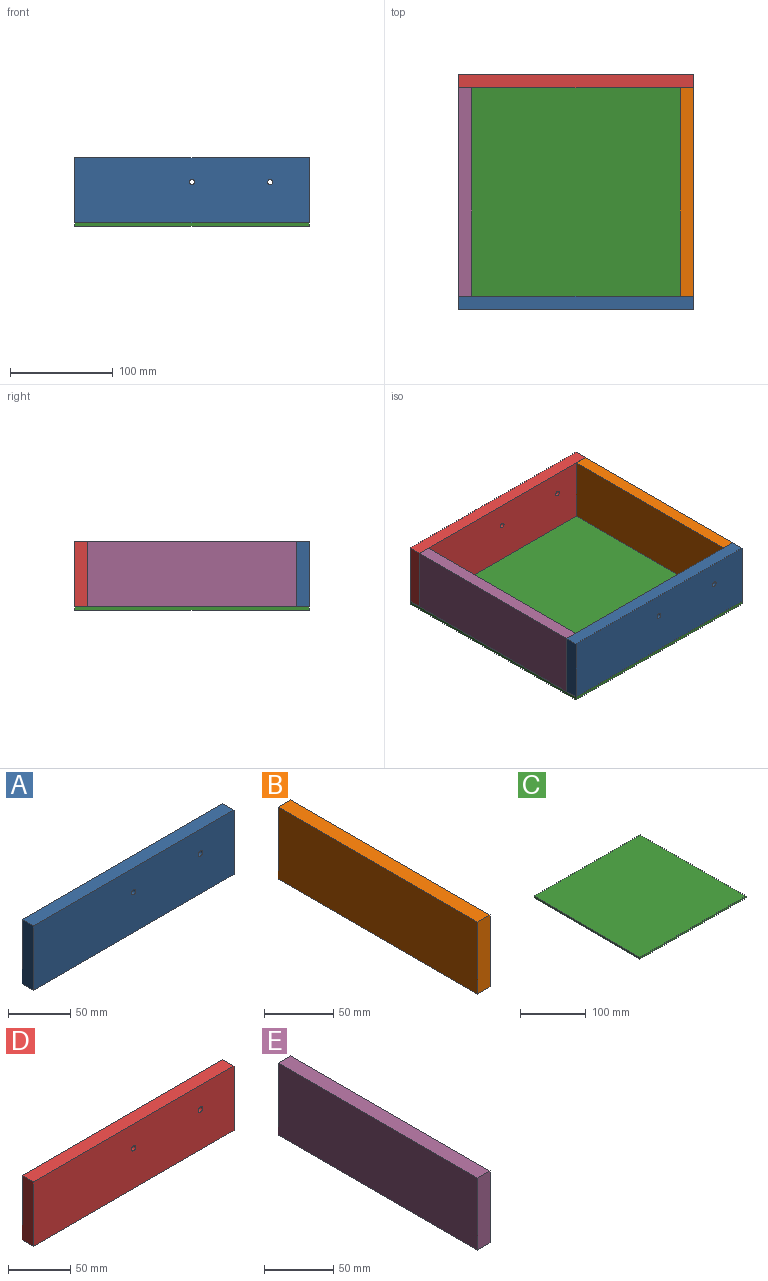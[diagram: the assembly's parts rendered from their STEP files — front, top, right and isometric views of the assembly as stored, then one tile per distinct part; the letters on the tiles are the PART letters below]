
ASSEMBLY  parts=5 mates=4
PART A: 8 faces, bbox 228.6x12.7x63.5 mm
  f0: plane 228.6x63.5mm, normal (0,1,0), area 14476.8mm2, adj f1,f3,f4,f5,f6,f7
  f1: plane 63.5x12.7mm, normal (-1,0,0), area 806.5mm2, adj f0,f2,f4,f5
  f2: plane 228.6x63.5mm, normal (0,-1,0), area 14476.8mm2, adj f1,f3,f4,f5,f6,f7
  f3: plane 63.5x12.7mm, normal (1,0,0), area 806.5mm2, adj f0,f2,f4,f5
  f4: plane 228.6x12.7mm, normal (0,0,1), area 2903.2mm2, adj f0,f1,f2,f3
  f5: plane 228.6x12.7mm, normal (0,0,-1), area 2903.2mm2, adj f0,f1,f2,f3
  f6: cylinder r=2.5mm len=12.7mm, axis (0,-1,0), area 199.5mm2, adj f0,f2
  f7: cylinder r=2.5mm len=12.7mm, axis (0,-1,0), area 199.5mm2, adj f0,f2
PART B: 6 faces, bbox 12.7x203.2x63.5 mm
  f0: plane 63.5x12.7mm, normal (0,1,0), area 806.5mm2, adj f1,f3,f4,f5
  f1: plane 203.2x63.5mm, normal (-1,0,0), area 12903.2mm2, adj f0,f2,f4,f5
  f2: plane 63.5x12.7mm, normal (0,-1,0), area 806.5mm2, adj f1,f3,f4,f5
  f3: plane 203.2x63.5mm, normal (1,0,0), area 12903.2mm2, adj f0,f2,f4,f5
  f4: plane 203.2x12.7mm, normal (0,0,1), area 2580.6mm2, adj f0,f1,f2,f3
  f5: plane 203.2x12.7mm, normal (0,0,-1), area 2580.6mm2, adj f0,f1,f2,f3
PART C: 6 faces, bbox 228.6x228.6x3.2 mm
  f0: plane 228.6x3.18mm, normal (0,-1,0), area 725.8mm2, adj f1,f3,f4,f5
  f1: plane 228.6x3.18mm, normal (1,0,0), area 725.8mm2, adj f0,f2,f4,f5
  f2: plane 228.6x3.18mm, normal (0,1,0), area 725.8mm2, adj f1,f3,f4,f5
  f3: plane 228.6x3.18mm, normal (-1,0,0), area 725.8mm2, adj f0,f2,f4,f5
  f4: plane 228.6x228.6mm, normal (0,0,1), area 52258mm2, adj f0,f1,f2,f3
  f5: plane 228.6x228.6mm, normal (0,0,-1), area 52258mm2, adj f0,f1,f2,f3
PART D: 8 faces, bbox 228.6x12.7x63.5 mm
  f0: plane 63.5x12.7mm, normal (-1,0,0), area 806.4mm2, adj f1,f3,f4,f5
  f1: plane 228.6x63.5mm, normal (0,-1,0), area 14476.8mm2, adj f0,f2,f4,f5,f6,f7
  f2: plane 63.5x12.7mm, normal (1,0,0), area 806.5mm2, adj f1,f3,f4,f5
  f3: plane 228.6x63.5mm, normal (0,1,0), area 14476.8mm2, adj f0,f2,f4,f5,f6,f7
  f4: plane 228.6x12.7mm, normal (0,0,1), area 2903.2mm2, adj f0,f1,f2,f3
  f5: plane 228.6x12.7mm, normal (0,0,-1), area 2903.2mm2, adj f0,f1,f2,f3
  f6: cylinder r=2.5mm len=12.7mm, axis (0,-1,0), area 199.5mm2, adj f1,f3
  f7: cylinder r=2.5mm len=12.7mm, axis (0,-1,0), area 199.5mm2, adj f1,f3
PART E: 6 faces, bbox 12.7x203.2x63.5 mm
  f0: plane 203.2x63.5mm, normal (1,0,0), area 12903.2mm2, adj f1,f3,f4,f5
  f1: plane 63.5x12.7mm, normal (0,1,0), area 806.4mm2, adj f0,f2,f4,f5
  f2: plane 203.2x63.5mm, normal (-1,0,0), area 12903.2mm2, adj f1,f3,f4,f5
  f3: plane 63.5x12.7mm, normal (0,-1,0), area 806.4mm2, adj f0,f2,f4,f5
  f4: plane 203.2x12.7mm, normal (0,0,1), area 2580.6mm2, adj f0,f1,f2,f3
  f5: plane 203.2x12.7mm, normal (0,0,-1), area 2580.6mm2, adj f0,f1,f2,f3
PLACE A at identity
PLACE B at identity
PLACE C at identity
PLACE D at identity
PLACE E at identity
MATE fastened D.f3 <-> C.f2  axis (0,1,0) through (-114.3,114.3,174.62)mm
MATE fastened A.f2 <-> C.f0  axis (0,-1,0) through (-114.3,-114.3,174.62)mm
MATE fastened B.f3 <-> C.f1  axis (1,0,0) through (0,0,174.62)mm
MATE fastened E.f2 <-> C.f3  axis (-1,0,0) through (-228.6,0,174.62)mm
